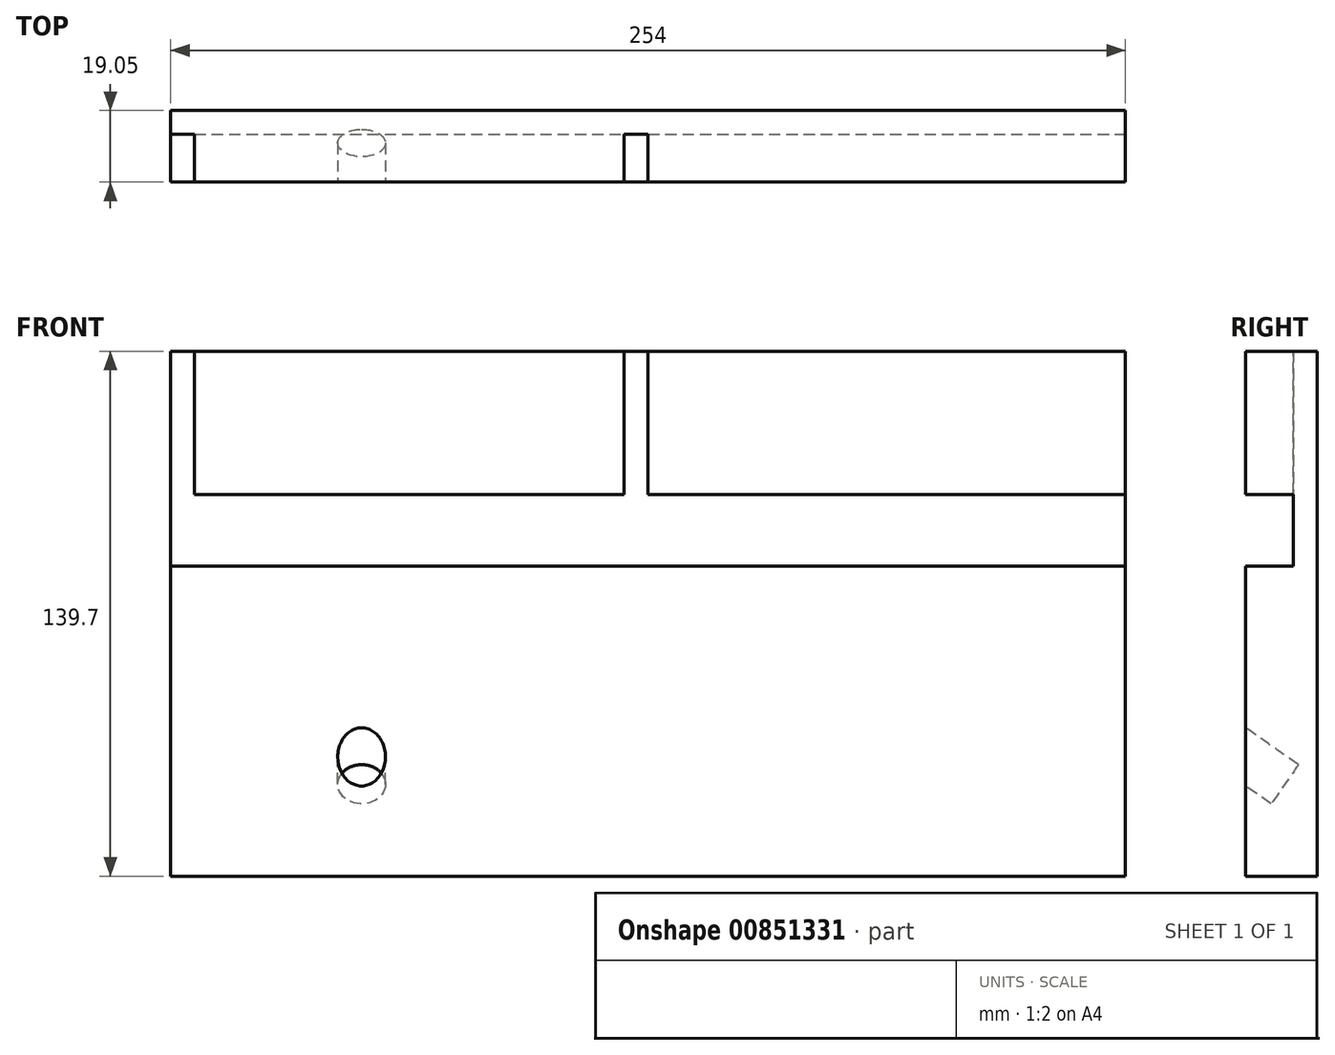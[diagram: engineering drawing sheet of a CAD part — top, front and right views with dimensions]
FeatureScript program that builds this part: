
annotation { "Feature Type Name" : "Feature", "Feature Type Description" : "" }
export const myFeature = defineFeature(function(context is Context, id is Id, definition is map)
    precondition{}
    {
        {
            var Q0;
            Q0=qCreatedBy(makeId("Front.planeOp"),FACE);
            var sketch = newSketch(context, id + "F0", { "sketchPlane" : qUnion([Q0])});
            skLineSegment(sketch, "E0.bottom", {"start": v(-127, 69.85) * mm, "end": v(127, 69.85) * mm});
            skLineSegment(sketch, "E0.top", {"start": v(-127, -69.85) * mm, "end": v(127, -69.85) * mm});
            skLineSegment(sketch, "E0.left", {"start": v(-127, 69.85) * mm, "end": v(-127, -69.85) * mm});
            skLineSegment(sketch, "E0.right", {"start": v(127, 69.85) * mm, "end": v(127, -69.85) * mm});
            skSolve(sketch);
        }
        {
            var Q0;
            Q0=makeQuery(id+"F0.imprint","IMPRINT",FACE,{"disambiguationData":[TD([[makeQuery(id+"F0.imprint","IMPRINT",EDGE,{"derivedFrom":sQuery(id+"F0.wireOp",EDGE,"E0.bottom")}),-1.0]])]});
            extrude(context, id + "F1", {"entities" : qUnion([Q0]), "depth" : 19.05 * mm, "offsetDistance" : 25.4 * mm});
        }
        {
            var Q0;
            Q0=makeQuery(id+"F1.opExtrude","CAP_FACE",FACE,{"disambiguationData":[OSD([sQuery(id+"F0.wireOp",EDGE,"E0.bottom"),sQuery(id+"F0.wireOp",EDGE,"E0.top"),sQuery(id+"F0.wireOp",EDGE,"E0.left"),sQuery(id+"F0.wireOp",EDGE,"E0.right")])],"isStart":false});
            var sketch = newSketch(context, id + "F2", { "sketchPlane" : qUnion([Q0])});
            skLineSegment(sketch, "E1.bottom", {"start": v(-127, 31.75) * mm, "end": v(127, 31.75) * mm});
            skLineSegment(sketch, "E1.top", {"start": v(-127, 12.7) * mm, "end": v(127, 12.7) * mm});
            skLineSegment(sketch, "E1.left", {"start": v(-127, 31.75) * mm, "end": v(-127, 12.7) * mm});
            skLineSegment(sketch, "E1.right", {"start": v(127, 31.75) * mm, "end": v(127, 12.7) * mm});
            skSolve(sketch);
        }
        {
            var Q0;
            Q0 = qSketchRegion(id + "F2", true);
            var Q1;
            Q1=makeQuery(id+"F2.imprint","IMPRINT",FACE,{"disambiguationData":[TD([[makeQuery(id+"F2.imprint","IMPRINT",EDGE,{"derivedFrom":sQuery(id+"F2.wireOp",EDGE,"E1.bottom")}),-1.0]])]});
            extrude(context, id + "F3", {"entities" : qUnion([Q0, Q1]), "operationType" : NewBodyOperationType.REMOVE, "oppositeDirection" : true, "depth" : 12.7 * mm, "offsetDistance" : 25.4 * mm});
        }
        {
            var Q0;
            {var subQ0=sQuery(id+"F0.wireOp",EDGE,"E0.bottom");var subQ1=sQuery(id+"F0.wireOp",EDGE,"E0.right");var subQ2=sQuery(id+"F0.wireOp",EDGE,"E0.left");Q0=makeQuery(id+"F3.boolean.opBoolean","SPLIT",FACE,{"disambiguationData":[TD([makeQuery(id+"F1.opExtrude","SWEPT_FACE",FACE,{"disambiguationData":[OSD([subQ0])]})])],"derivedFrom":makeQuery(id+"F1.opExtrude","CAP_FACE",FACE,{"disambiguationData":[OSD([subQ0,sQuery(id+"F0.wireOp",EDGE,"E0.top"),subQ2,subQ1])],"isStart":false})});}
            var sketch = newSketch(context, id + "F4", { "sketchPlane" : qUnion([Q0])});
            skLineSegment(sketch, "E2.bottom", {"start": v(-127, 31.75) * mm, "end": v(-120.65, 31.75) * mm});
            skLineSegment(sketch, "E2.top", {"start": v(-127, 69.85) * mm, "end": v(-120.65, 69.85) * mm});
            skLineSegment(sketch, "E2.left", {"start": v(-127, 31.75) * mm, "end": v(-127, 69.85) * mm});
            skLineSegment(sketch, "E2.right", {"start": v(-120.65, 31.75) * mm, "end": v(-120.65, 69.85) * mm});
            skLineSegment(sketch, "E3.bottom", {"start": v(-6.35, 31.75) * mm, "end": v(0, 31.75) * mm});
            skLineSegment(sketch, "E3.top", {"start": v(-6.35, 69.85) * mm, "end": v(0, 69.85) * mm});
            skLineSegment(sketch, "E3.left", {"start": v(-6.35, 31.75) * mm, "end": v(-6.35, 69.85) * mm});
            skLineSegment(sketch, "E3.right", {"start": v(0, 31.75) * mm, "end": v(0, 69.85) * mm});
            skSolve(sketch);
        }
        {
            var Q0;
            Q0=makeQuery(id+"F4.imprint","IMPRINT",FACE,{"disambiguationData":[TD([[makeQuery(id+"F4.imprint","IMPRINT",EDGE,{"derivedFrom":sQuery(id+"F4.wireOp",EDGE,"E3.bottom")}),1.0]])]});
            var Q1;
            Q1=makeQuery(id+"F4.imprint","IMPRINT",FACE,{"disambiguationData":[TD([[makeQuery(id+"F4.imprint","IMPRINT",EDGE,{"derivedFrom":sQuery(id+"F4.wireOp",EDGE,"E2.bottom")}),1.0]])]});
            extrude(context, id + "F5", {"entities" : qUnion([Q0, Q1]), "operationType" : NewBodyOperationType.REMOVE, "oppositeDirection" : true, "depth" : 12.7 * mm, "offsetDistance" : 25.4 * mm});
        }
        {
            var Q0;
            {var subQ0=sQuery(id+"F0.wireOp",EDGE,"E0.top");var subQ1=sQuery(id+"F0.wireOp",EDGE,"E0.left");var subQ2=sQuery(id+"F0.wireOp",EDGE,"E0.right");Q0=makeQuery(id+"F3.boolean.opBoolean","SPLIT",FACE,{"disambiguationData":[TD([makeQuery(id+"F1.opExtrude","SWEPT_FACE",FACE,{"disambiguationData":[OSD([subQ0])]})])],"derivedFrom":makeQuery(id+"F1.opExtrude","CAP_FACE",FACE,{"disambiguationData":[OSD([sQuery(id+"F0.wireOp",EDGE,"E0.bottom"),subQ0,subQ1,subQ2])],"isStart":false})});}
            var sketch = newSketch(context, id + "F6", { "sketchPlane" : qUnion([Q0])});
            skLineSegment(sketch, "E4", {"start": v(-127, -38.1) * mm, "end": v(127, -38.1) * mm});
            skLineSegment(sketch, "E5", {"start": v(-76.2, -38.1) * mm, "end": v(-76.2, -69.85) * mm});
            skLineSegment(sketch, "E6", {"start": v(76.2, -38.1) * mm, "end": v(76.2, -69.85) * mm});
            skSolve(sketch);
        }
        {
            var Q0;
            Q0=sQuery(id+"F6.wireOp",EDGE,"E4");
            var Q1;
            Q1=sQuery(id+"F6.wireOp",EDGE,"E4");
            var Q2;
            Q2=sQuery(id+"F6.wireOp",EDGE,"E4");
            var Q3;
            Q3=sQuery(id+"F6.wireOp",EDGE,"E4");
            cPlane(context, id + "F7", {"entities" : qUnion([Q0, Q1, Q2, Q3]), "cplaneType" : CPlaneType.LINE_ANGLE, "offset" : 25.4 * mm, "angle" : 35 * degree, "oppositeDirection" : true, "width" : 152.4 * mm, "height" : 152.4 * mm});
        }
        {
            var Q0;
            Q0=qCreatedBy(id+"F7.planeOp",FACE);
            var Q1;
            Q1=qCreatedBy(id+"F7.planeOp",FACE);
            var Q2;
            Q2=qCreatedBy(id+"F7.planeOp",FACE);
            var Q3;
            Q3=qCreatedBy(id+"F7.planeOp",FACE);
            var Q4;
            Q4=qCreatedBy(id+"F7.planeOp",FACE);
            var sketch = newSketch(context, id + "F8", { "sketchPlane" : qUnion([Q0, Q1, Q2, Q3, Q4])});
            skCircle(sketch, "E7", {"center": v(76.2, -42.14) * mm, "radius": 6.35 * mm});
            skSolve(sketch);
        }
        {
            var Q0;
            Q0=makeQuery(id+"F8.imprint","IMPRINT",FACE,{"disambiguationData":[TD([[makeQuery(id+"F8.imprint","IMPRINT",EDGE,{"derivedFrom":sQuery(id+"F8.wireOp",EDGE,"E7")}),1.0]])]});
            var Q1;
            Q1=makeQuery(id+"F8.imprint","IMPRINT",FACE,{"disambiguationData":[TD([[makeQuery(id+"F8.imprint","IMPRINT",EDGE,{"derivedFrom":sQuery(id+"F8.wireOp",EDGE,"E7")}),1.0]])]});
            var Q2;
            Q2=makeQuery(id+"F8.imprint","IMPRINT",FACE,{"disambiguationData":[TD([[makeQuery(id+"F8.imprint","IMPRINT",EDGE,{"derivedFrom":sQuery(id+"F8.wireOp",EDGE,"E7")}),1.0]])]});
            var Q3;
            Q3=makeQuery(id+"F8.imprint","IMPRINT",FACE,{"disambiguationData":[TD([[makeQuery(id+"F8.imprint","IMPRINT",EDGE,{"derivedFrom":sQuery(id+"F8.wireOp",EDGE,"E7")}),1.0]])]});
            var Q4;
            Q4=makeQuery(id+"F8.imprint","IMPRINT",FACE,{"disambiguationData":[TD([[makeQuery(id+"F8.imprint","IMPRINT",EDGE,{"derivedFrom":sQuery(id+"F8.wireOp",EDGE,"E7")}),1.0]])]});
            extrude(context, id + "F9", {"entities" : qUnion([Q0, Q1, Q2, Q3, Q4]), "operationType" : NewBodyOperationType.REMOVE, "depth" : 12.7 * mm, "offsetDistance" : 25.4 * mm, "hasSecondDirection" : true, "secondDirectionOppositeDirection" : true, "secondDirectionDepth" : 12.7 * mm});
        }
    });
